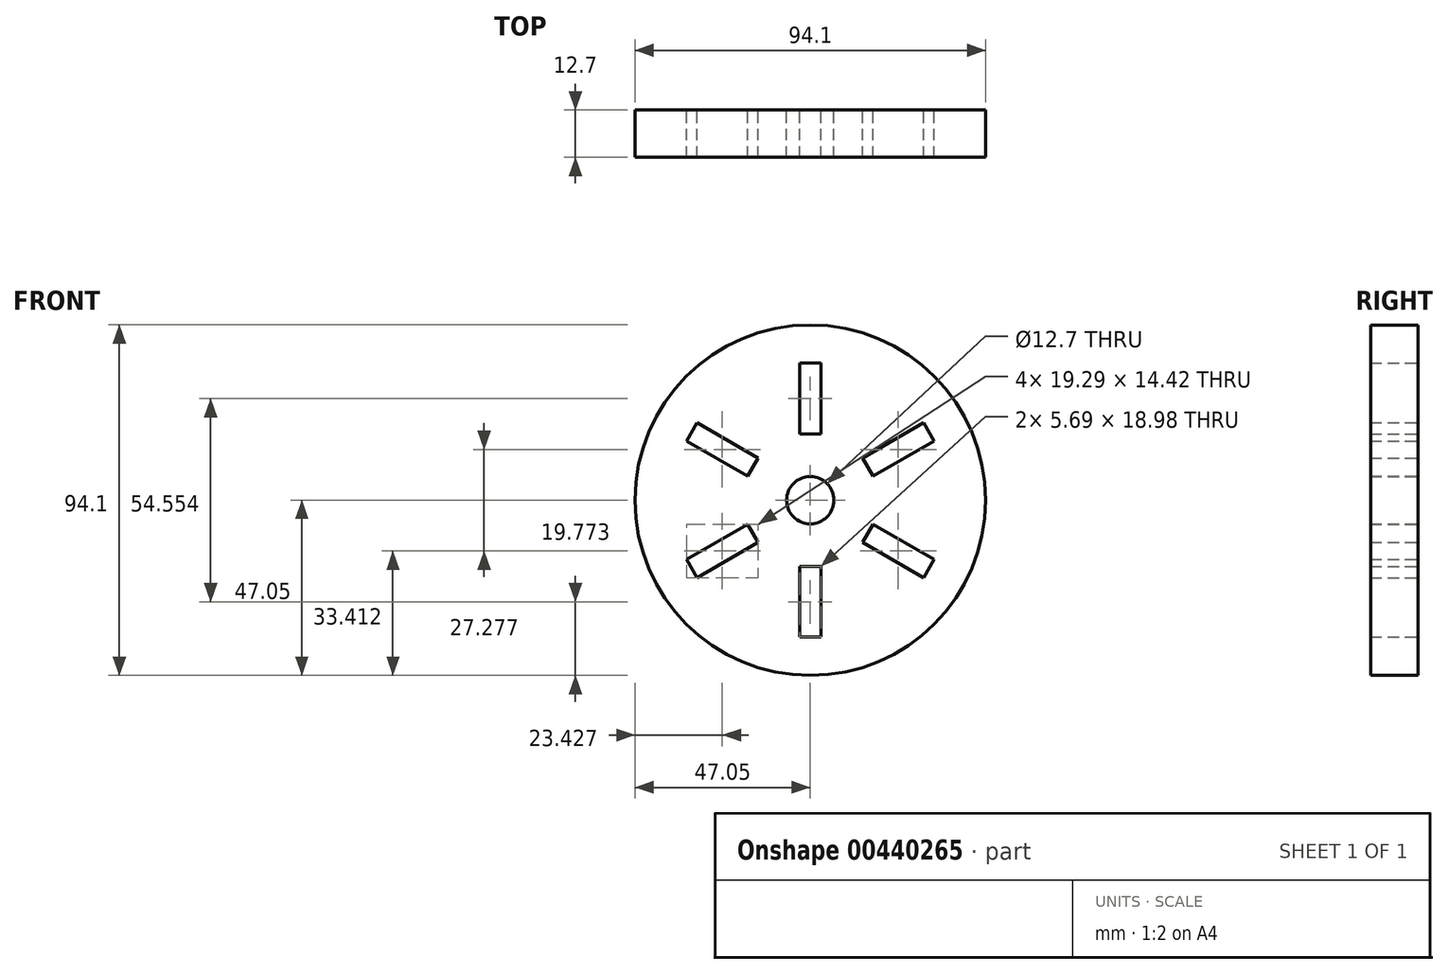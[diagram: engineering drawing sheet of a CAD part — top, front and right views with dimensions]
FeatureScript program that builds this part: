
annotation { "Feature Type Name" : "Feature", "Feature Type Description" : "" }
export const myFeature = defineFeature(function(context is Context, id is Id, definition is map)
    precondition{}
    {
        {
            var Q0;
            Q0=qCreatedBy(makeId("Front.planeOp"),FACE);
            var sketch = newSketch(context, id + "F0", { "sketchPlane" : qUnion([Q0])});
            skCircle(sketch, "E0", {"center": v(0, 0) * mm, "radius": 47.05 * mm});
            skLineSegment(sketch, "E1.bottom", {"start": v(2.84, 17.78) * mm, "end": v(-2.84, 17.78) * mm});
            skLineSegment(sketch, "E1.top", {"start": v(2.84, 36.77) * mm, "end": v(-2.84, 36.77) * mm});
            skLineSegment(sketch, "E1.left", {"start": v(2.84, 17.78) * mm, "end": v(2.84, 36.77) * mm});
            skLineSegment(sketch, "E1.right", {"start": v(-2.84, 17.78) * mm, "end": v(-2.84, 36.77) * mm});
            skPoint(sketch, "E1.middle", {"position": v(0, 27.28) * mm});
            skLineSegment(sketch, "E2.1.0", {"start": v(16.82, 6.43) * mm, "end": v(33.27, 15.92) * mm});
            skLineSegment(sketch, "E2.1.1", {"start": v(13.98, 11.36) * mm, "end": v(30.42, 20.85) * mm});
            skPoint(sketch, "E2.1.2", {"position": v(23.62, 13.64) * mm});
            skLineSegment(sketch, "E2.1.3", {"start": v(16.82, 6.43) * mm, "end": v(13.98, 11.36) * mm});
            skLineSegment(sketch, "E2.1.4", {"start": v(33.27, 15.92) * mm, "end": v(30.42, 20.85) * mm});
            skLineSegment(sketch, "E2.2.0", {"start": v(13.98, -11.36) * mm, "end": v(30.42, -20.85) * mm});
            skLineSegment(sketch, "E2.2.1", {"start": v(16.82, -6.43) * mm, "end": v(33.27, -15.92) * mm});
            skPoint(sketch, "E2.2.2", {"position": v(23.62, -13.64) * mm});
            skLineSegment(sketch, "E2.2.3", {"start": v(13.98, -11.36) * mm, "end": v(16.82, -6.43) * mm});
            skLineSegment(sketch, "E2.2.4", {"start": v(30.42, -20.85) * mm, "end": v(33.27, -15.92) * mm});
            skLineSegment(sketch, "E2.3.0", {"start": v(-2.84, -17.78) * mm, "end": v(-2.84, -36.77) * mm});
            skLineSegment(sketch, "E2.3.1", {"start": v(2.84, -17.78) * mm, "end": v(2.84, -36.77) * mm});
            skPoint(sketch, "E2.3.2", {"position": v(0, -27.28) * mm});
            skLineSegment(sketch, "E2.3.3", {"start": v(-2.84, -17.78) * mm, "end": v(2.84, -17.78) * mm});
            skLineSegment(sketch, "E2.3.4", {"start": v(-2.84, -36.77) * mm, "end": v(2.84, -36.77) * mm});
            skLineSegment(sketch, "E2.4.0", {"start": v(-16.82, -6.43) * mm, "end": v(-33.27, -15.92) * mm});
            skLineSegment(sketch, "E2.4.1", {"start": v(-13.98, -11.36) * mm, "end": v(-30.42, -20.85) * mm});
            skPoint(sketch, "E2.4.2", {"position": v(-23.62, -13.64) * mm});
            skLineSegment(sketch, "E2.4.3", {"start": v(-16.82, -6.43) * mm, "end": v(-13.98, -11.36) * mm});
            skLineSegment(sketch, "E2.4.4", {"start": v(-33.27, -15.92) * mm, "end": v(-30.42, -20.85) * mm});
            skLineSegment(sketch, "E2.5.0", {"start": v(-13.98, 11.36) * mm, "end": v(-30.42, 20.85) * mm});
            skLineSegment(sketch, "E2.5.1", {"start": v(-16.82, 6.43) * mm, "end": v(-33.27, 15.92) * mm});
            skPoint(sketch, "E2.5.2", {"position": v(-23.62, 13.64) * mm});
            skLineSegment(sketch, "E2.5.3", {"start": v(-13.98, 11.36) * mm, "end": v(-16.82, 6.43) * mm});
            skLineSegment(sketch, "E2.5.4", {"start": v(-30.42, 20.85) * mm, "end": v(-33.27, 15.92) * mm});
            skCircle(sketch, "E3", {"center": v(0, 0) * mm, "radius": 6.35 * mm});
            skSolve(sketch);
        }
        {
            var Q0;
            Q0=makeQuery(id+"F0.imprint","IMPRINT",FACE,{"disambiguationData":[TD([[makeQuery(id+"F0.imprint","IMPRINT",EDGE,{"derivedFrom":sQuery(id+"F0.wireOp",EDGE,"E0")}),1.0]])]});
            extrude(context, id + "F1", {"entities" : qUnion([Q0]), "depth" : 12.7 * mm});
        }
    });
